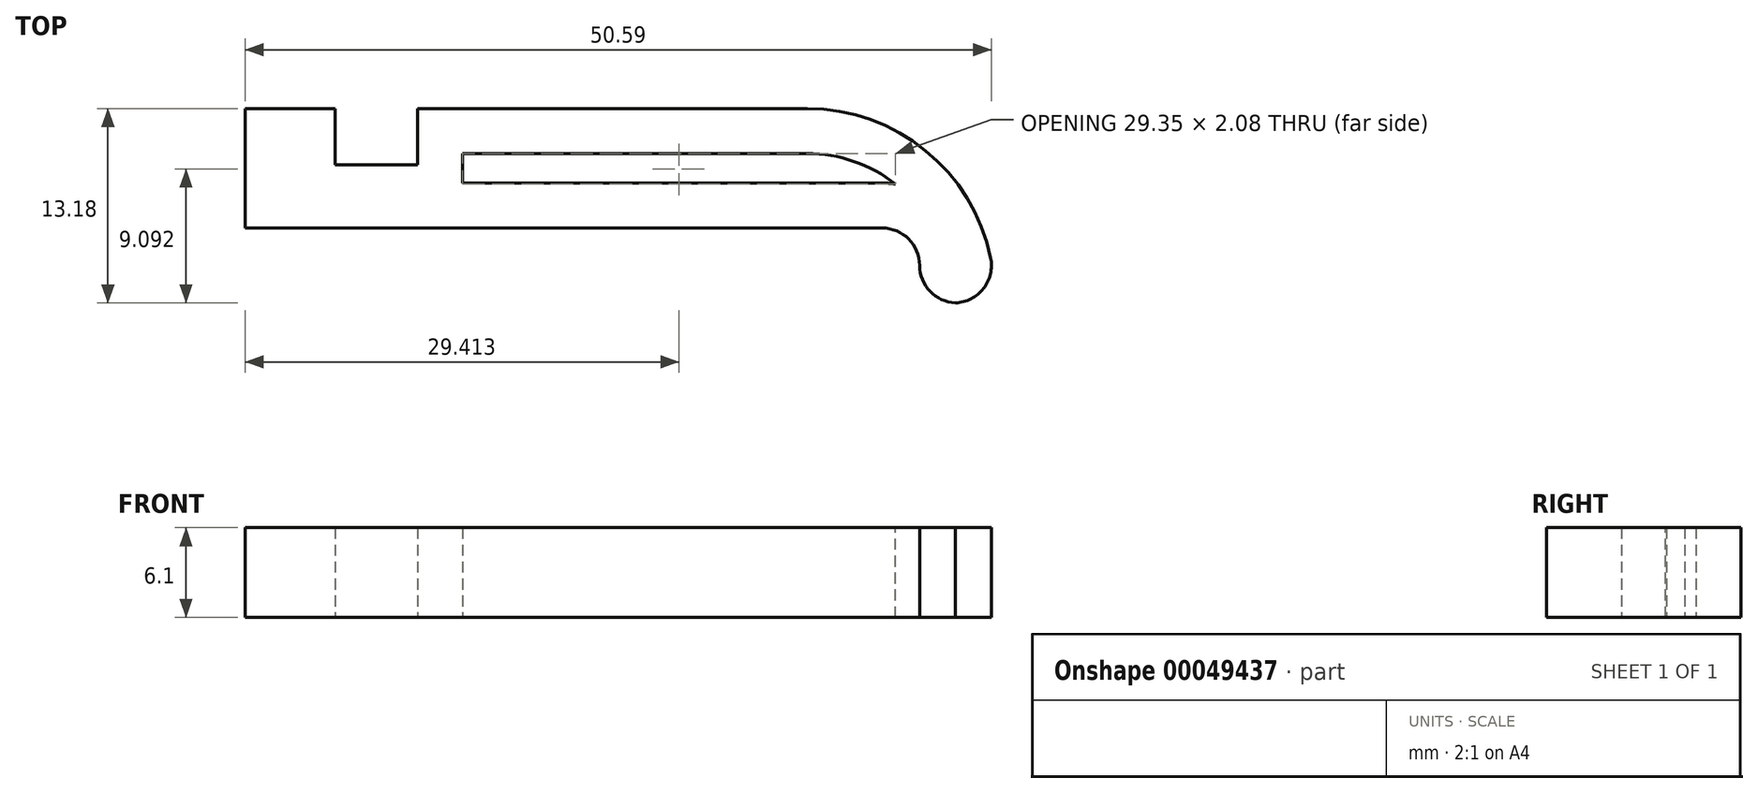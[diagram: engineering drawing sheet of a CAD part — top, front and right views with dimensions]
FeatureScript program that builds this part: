
annotation { "Feature Type Name" : "Feature", "Feature Type Description" : "" }
export const myFeature = defineFeature(function(context is Context, id is Id, definition is map)
    precondition{}
    {
        {
            var Q0;
            Q0=qCreatedBy(makeId("Top.planeOp"),FACE);
            var sketch = newSketch(context, id + "F0", { "sketchPlane" : qUnion([Q0])});
            skLineSegment(sketch, "E0", {"start": v(0, 0) * mm, "end": v(0, -3.81) * mm});
            skLineSegment(sketch, "E1", {"start": v(0, -3.81) * mm, "end": v(5.59, -3.8) * mm});
            skLineSegment(sketch, "E2", {"start": v(5.59, -3.81) * mm, "end": v(5.59, 0) * mm});
            skLineSegment(sketch, "E3", {"start": v(5.59, 0) * mm, "end": v(44.7, 0) * mm});
            skLineSegment(sketch, "E4", {"start": v(44.7, 0) * mm, "end": v(44.7, -8.1) * mm});
            skLineSegment(sketch, "E5", {"start": v(44.7, -8.1) * mm, "end": v(-6.1, -8.1) * mm});
            skLineSegment(sketch, "E6", {"start": v(-6.1, -8.1) * mm, "end": v(-6.1, 0) * mm});
            skLineSegment(sketch, "E7", {"start": v(-6.1, 0) * mm, "end": v(0, 0) * mm});
            skLineSegment(sketch, "E8", {"start": v(44.7, -8.1) * mm, "end": v(44.7, -13.18) * mm});
            skLineSegment(sketch, "E9", {"start": v(44.7, -13.18) * mm, "end": v(39.62, -13.18) * mm});
            skLineSegment(sketch, "E10", {"start": v(39.62, -13.18) * mm, "end": v(39.62, -8.1) * mm});
            skSolve(sketch);
        }
        {
            var Q0;
            Q0=makeQuery(id+"F0.imprint","IMPRINT",FACE,{"disambiguationData":[TD([[makeQuery(id+"F0.imprint","IMPRINT",EDGE,{"derivedFrom":sQuery(id+"F0.wireOp",EDGE,"E0")}),-1.0]])]});
            var Q1;
            {var subQ1=sQuery(id+"F0.wireOp",EDGE,"E8");Q1=makeQuery(id+"F0.imprint","IMPRINT",FACE,{"disambiguationData":[TD([[makeQuery(id+"F0.imprint","IMPRINT",EDGE,{"derivedFrom":subQ1}),-1.0]])]});}
            extrude(context, id + "F1", {"entities" : qUnion([Q0, Q1]), "depth" : 6.1 * mm});
        }
        {
            var Q0;
            Q0=makeQuery(id+"F1.opExtrude","SWEPT_EDGE",EDGE,{"disambiguationData":[OSD([sQuery(id+"F0.wireOp",EDGE,"E3"),sQuery(id+"F0.wireOp",EDGE,"E4")])]});
            fillet(context, id + "F2", {"entities" : qUnion([Q0]), "radius" : 12.7 * mm, "tangentPropagation" : true, "allowEdgeOverflow" : false});
        }
        {
            var Q0;
            Q0=makeQuery(id+"F1.opExtrude","SWEPT_EDGE",EDGE,{"disambiguationData":[OSD([sQuery(id+"F0.wireOp",EDGE,"E9"),sQuery(id+"F0.wireOp",EDGE,"E10")])]});
            var Q1;
            Q1=makeQuery(id+"F1.opExtrude","SWEPT_EDGE",EDGE,{"disambiguationData":[OSD([sQuery(id+"F0.wireOp",EDGE,"E8"),sQuery(id+"F0.wireOp",EDGE,"E9")])]});
            var Q2;
            Q2=makeQuery(id+"F1.opExtrude","SWEPT_EDGE",EDGE,{"disambiguationData":[OSD([sQuery(id+"F0.wireOp",EDGE,"E5"),sQuery(id+"F0.wireOp",EDGE,"E10")])]});
            fillet(context, id + "F3", {"entities" : qUnion([Q0, Q1, Q2]), "radius" : 2.54 * mm, "tangentPropagation" : true, "allowEdgeOverflow" : false});
        }
        {
            var Q0;
            Q0=makeQuery(id+"F1.opExtrude","CAP_FACE",FACE,{"disambiguationData":[OSD([sQuery(id+"F0.wireOp",EDGE,"E0"),sQuery(id+"F0.wireOp",EDGE,"E1"),sQuery(id+"F0.wireOp",EDGE,"E2"),sQuery(id+"F0.wireOp",EDGE,"E3"),sQuery(id+"F0.wireOp",EDGE,"E4"),sQuery(id+"F0.wireOp",EDGE,"E5"),sQuery(id+"F0.wireOp",EDGE,"E6"),sQuery(id+"F0.wireOp",EDGE,"E7"),sQuery(id+"F0.wireOp",EDGE,"E8"),sQuery(id+"F0.wireOp",EDGE,"E9"),sQuery(id+"F0.wireOp",EDGE,"E10")])],"isStart":false});
            shell(context, id + "F4", {"entities" : qUnion([Q0]), "thickness" : 3.05 * mm});
        }
        {
            var Q0;
            Q0=makeQuery(id+"F4.opShell","OFFSET_FACE",FACE,{"disambiguationData":[OSD([sQuery(id+"F0.wireOp",EDGE,"E0"),sQuery(id+"F0.wireOp",EDGE,"E1"),sQuery(id+"F0.wireOp",EDGE,"E2"),sQuery(id+"F0.wireOp",EDGE,"E3"),sQuery(id+"F0.wireOp",EDGE,"E4"),sQuery(id+"F0.wireOp",EDGE,"E5"),sQuery(id+"F0.wireOp",EDGE,"E6"),sQuery(id+"F0.wireOp",EDGE,"E7"),sQuery(id+"F0.wireOp",EDGE,"E8"),sQuery(id+"F0.wireOp",EDGE,"E9"),sQuery(id+"F0.wireOp",EDGE,"E10")])]});
            extrude(context, id + "F5", {"entities" : qUnion([Q0]), "operationType" : NewBodyOperationType.REMOVE, "oppositeDirection" : true, "depth" : 25.4 * mm});
        }
    });
